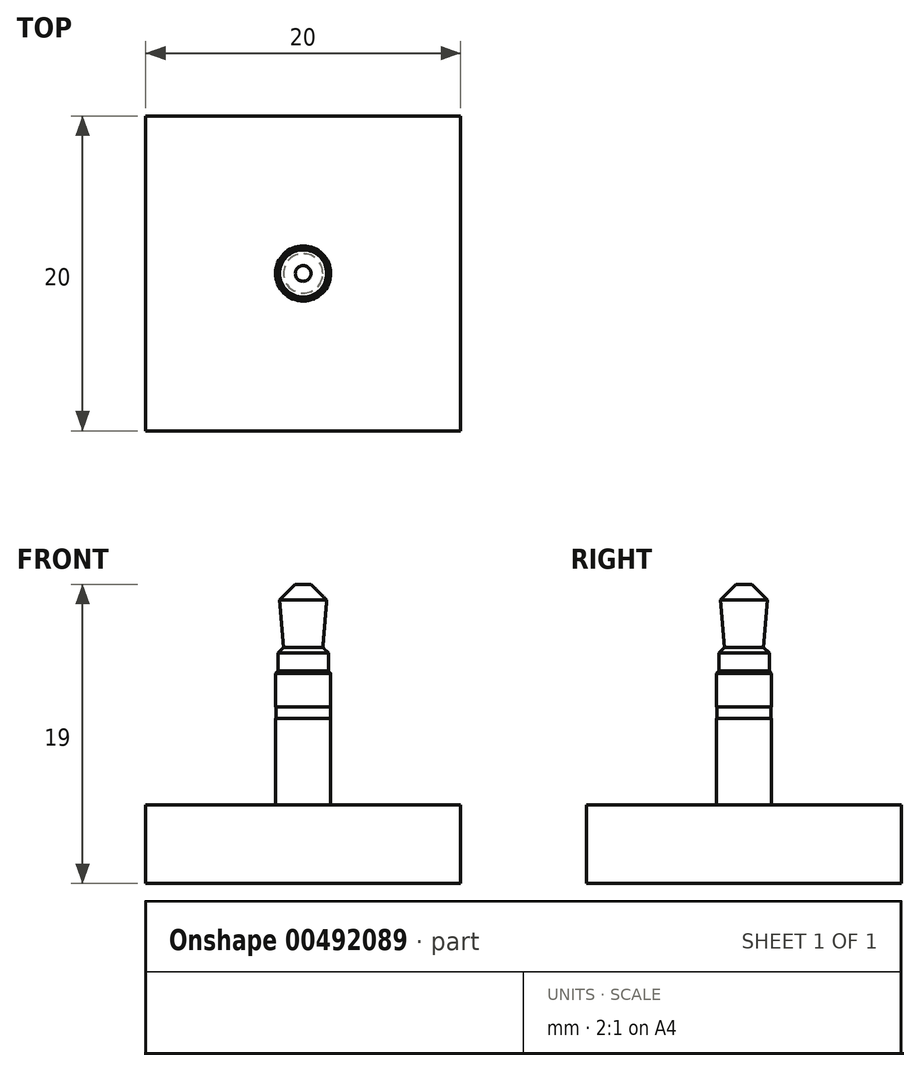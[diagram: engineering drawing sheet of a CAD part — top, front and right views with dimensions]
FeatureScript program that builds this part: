
annotation { "Feature Type Name" : "Feature", "Feature Type Description" : "" }
export const myFeature = defineFeature(function(context is Context, id is Id, definition is map)
    precondition{}
    {
        {
            var Q0;
            Q0=qCreatedBy(makeId("Top.planeOp"),FACE);
            var sketch = newSketch(context, id + "F0", { "sketchPlane" : qUnion([Q0])});
            skCircle(sketch, "E0", {"center": v(0, 0) * mm, "radius": 1.75 * mm});
            skSolve(sketch);
        }
        {
            var Q0;
            Q0=qSketchRegion(id+"F0",true);
            extrude(context, id + "F1", {"entities" : qUnion([Q0]), "depth" : 5.5 * mm});
        }
        {
            var Q0;
            Q0=makeQuery(id+"F1.opExtrude","CAP_FACE",FACE,{"disambiguationData":[OSD([sQuery(id+"F0.wireOp",EDGE,"E0")])],"isStart":false});
            cPlane(context, id + "F2", {"entities" : qUnion([Q0]), "cplaneType" : CPlaneType.OFFSET, "offset" : 0 * mm, "width" : 150 * mm, "height" : 150 * mm});
        }
        {
            var Q0;
            Q0=qCreatedBy(id+"F2.planeOp",FACE);
            var sketch = newSketch(context, id + "F3", { "sketchPlane" : qUnion([Q0])});
            skCircle(sketch, "E1", {"center": v(0, 0) * mm, "radius": 1.73 * mm});
            skSolve(sketch);
        }
        {
            var Q0;
            Q0=qSketchRegion(id+"F3",true);
            extrude(context, id + "F4", {"entities" : qUnion([Q0]), "operationType" : NewBodyOperationType.ADD, "depth" : 0.7 * mm});
        }
        {
            var Q0;
            Q0=makeQuery(id+"F4.opExtrude","CAP_FACE",FACE,{"disambiguationData":[OSD([sQuery(id+"F3.wireOp",EDGE,"E1")])],"isStart":false});
            cPlane(context, id + "F5", {"entities" : qUnion([Q0]), "cplaneType" : CPlaneType.OFFSET, "offset" : 0 * mm, "width" : 150 * mm, "height" : 150 * mm});
        }
        {
            var Q0;
            Q0=qCreatedBy(id+"F5.planeOp",FACE);
            var sketch = newSketch(context, id + "F6", { "sketchPlane" : qUnion([Q0])});
            skCircle(sketch, "E2", {"center": v(0, 0) * mm, "radius": 1.75 * mm});
            skSolve(sketch);
        }
        {
            var Q0;
            Q0=qSketchRegion(id+"F6",true);
            extrude(context, id + "F7", {"entities" : qUnion([Q0]), "operationType" : NewBodyOperationType.ADD, "depth" : 2.3 * mm});
        }
        {
            var Q0;
            Q0=makeQuery(id+"F7.opExtrude","CAP_FACE",FACE,{"disambiguationData":[OSD([sQuery(id+"F6.wireOp",EDGE,"E2")])],"isStart":false});
            cPlane(context, id + "F8", {"entities" : qUnion([Q0]), "cplaneType" : CPlaneType.OFFSET, "offset" : 0 * mm, "width" : 150 * mm, "height" : 150 * mm});
        }
        {
            var Q0;
            Q0=qCreatedBy(id+"F8.planeOp",FACE);
            var sketch = newSketch(context, id + "F9", { "sketchPlane" : qUnion([Q0])});
            skCircle(sketch, "E3", {"center": v(0, 0) * mm, "radius": 1.6 * mm});
            skSolve(sketch);
        }
        {
            var Q0;
            Q0=qSketchRegion(id+"F9",true);
            extrude(context, id + "F10", {"entities" : qUnion([Q0]), "operationType" : NewBodyOperationType.ADD, "depth" : 0.7 * mm});
        }
        {
            var Q0;
            Q0=makeQuery(id+"F10.opExtrude","CAP_FACE",FACE,{"disambiguationData":[OSD([sQuery(id+"F9.wireOp",EDGE,"E3")])],"isStart":false});
            cPlane(context, id + "F11", {"entities" : qUnion([Q0]), "cplaneType" : CPlaneType.OFFSET, "offset" : 0 * mm, "width" : 150 * mm, "height" : 150 * mm});
        }
        {
            var Q0;
            Q0=qCreatedBy(id+"F11.planeOp",FACE);
            var sketch = newSketch(context, id + "F12", { "sketchPlane" : qUnion([Q0])});
            skCircle(sketch, "E4", {"center": v(0, 0) * mm, "radius": 1.6 * mm});
            skSolve(sketch);
        }
        {
            var Q0;
            Q0=qSketchRegion(id+"F12",true);
            extrude(context, id + "F13", {"entities" : qUnion([Q0]), "operationType" : NewBodyOperationType.ADD, "depth" : 0.8 * mm});
        }
        {
            var Q0;
            Q0=makeQuery(id+"F13.opExtrude","CAP_FACE",FACE,{"disambiguationData":[OSD([sQuery(id+"F12.wireOp",EDGE,"E4")])],"isStart":false});
            cPlane(context, id + "F14", {"entities" : qUnion([Q0]), "cplaneType" : CPlaneType.OFFSET, "offset" : 0 * mm, "width" : 150 * mm, "height" : 150 * mm});
        }
        {
            var Q0;
            Q0=qCreatedBy(id+"F14.planeOp",FACE);
            var sketch = newSketch(context, id + "F15", { "sketchPlane" : qUnion([Q0])});
            skCircle(sketch, "E5", {"center": v(0, 0) * mm, "radius": 1.25 * mm});
            skSolve(sketch);
        }
        {
            var Q0;
            Q0=makeQuery(id+"F15.imprint","IMPRINT",FACE,{"disambiguationData":[TD([[makeQuery(id+"F15.imprint","IMPRINT",EDGE,{"derivedFrom":sQuery(id+"F15.wireOp",EDGE,"E5")}),1.0]])]});
            cPlane(context, id + "F16", {"entities" : qUnion([Q0]), "cplaneType" : CPlaneType.OFFSET, "offset" : 3 * mm, "width" : 150 * mm, "height" : 150 * mm});
        }
        {
            var Q0;
            Q0=qCreatedBy(id+"F16.planeOp",FACE);
            var sketch = newSketch(context, id + "F17", { "sketchPlane" : qUnion([Q0])});
            skCircle(sketch, "E6", {"center": v(0, 0) * mm, "radius": 1.5 * mm});
            skSolve(sketch);
        }
        {
            var Q1;
            Q1=makeQuery(id+"F15.imprint","IMPRINT",FACE,{"disambiguationData":[TD([[makeQuery(id+"F15.imprint","IMPRINT",EDGE,{"derivedFrom":sQuery(id+"F15.wireOp",EDGE,"E5")}),1.0]])]});
            var Q2;
            Q2=makeQuery(id+"F17.imprint","IMPRINT",FACE,{"disambiguationData":[TD([[makeQuery(id+"F17.imprint","IMPRINT",EDGE,{"derivedFrom":sQuery(id+"F17.wireOp",EDGE,"E6")}),1.0]])]});
            loft(context, id + "F18", {"operationType" : NewBodyOperationType.ADD, "sheetProfilesArray" : [{ "sheetProfileEntities" : qUnion([Q1]) }, { "sheetProfileEntities" : qUnion([Q2]) }]});
        }
        {
            var Q0;
            Q0=makeQuery(id+"F18.opLoft","CAP_FACE",FACE,{"disambiguationData":[OSD([makeQuery(id+"F17.imprint","IMPRINT",FACE,{"disambiguationData":[TD([[makeQuery(id+"F17.imprint","IMPRINT",EDGE,{"derivedFrom":sQuery(id+"F17.wireOp",EDGE,"E6")}),1.0]])]})])],"isStart":true});
            cPlane(context, id + "F19", {"entities" : qUnion([Q0]), "cplaneType" : CPlaneType.OFFSET, "offset" : 0 * mm, "width" : 150 * mm, "height" : 150 * mm});
        }
        {
            var Q0;
            Q0=qCreatedBy(id+"F19.planeOp",FACE);
            var sketch = newSketch(context, id + "F20", { "sketchPlane" : qUnion([Q0])});
            skCircle(sketch, "E7", {"center": v(0, 0) * mm, "radius": 1.5 * mm});
            skSolve(sketch);
        }
        {
            var Q0;
            Q0=qSketchRegion(id+"F20",true);
            extrude(context, id + "F21", {"entities" : qUnion([Q0]), "operationType" : NewBodyOperationType.ADD, "depth" : 1 * mm});
        }
        {
            var Q0;
            Q0=makeQuery(id+"F21.opExtrude","CAP_EDGE",EDGE,{"disambiguationData":[OSD([sQuery(id+"F20.wireOp",EDGE,"E7")])],"isStart":false});
            chamfer(context, id + "F22", {"entities" : qUnion([Q0]), "chamferType" : ChamferType.OFFSET_ANGLE, "width" : 1 * mm, "oppositeDirection" : false, "angle" : 45 * degree, "tangentPropagation" : true});
        }
        {
            var Q0;
            Q0=makeQuery(id+"F7.opExtrude","CAP_EDGE",EDGE,{"disambiguationData":[OSD([sQuery(id+"F6.wireOp",EDGE,"E2")])],"isStart":false});
            chamfer(context, id + "F23", {"entities" : qUnion([Q0]), "width" : 0.15 * mm, "tangentPropagation" : true});
        }
        {
            var Q0;
            Q0=makeQuery(id+"F13.opExtrude","CAP_EDGE",EDGE,{"disambiguationData":[OSD([sQuery(id+"F12.wireOp",EDGE,"E4")])],"isStart":false});
            chamfer(context, id + "F24", {"entities" : qUnion([Q0]), "width" : 0.35 * mm, "tangentPropagation" : true});
        }
        {
            var Q0;
            Q0=makeQuery(id+"F1.opExtrude","CAP_FACE",FACE,{"disambiguationData":[OSD([sQuery(id+"F0.wireOp",EDGE,"E0")])],"isStart":true});
            cPlane(context, id + "F25", {"entities" : qUnion([Q0]), "cplaneType" : CPlaneType.OFFSET, "offset" : 0 * mm, "width" : 150 * mm, "height" : 150 * mm});
        }
        {
            var Q0;
            Q0=qCreatedBy(id+"F25.planeOp",FACE);
            var sketch = newSketch(context, id + "F26", { "sketchPlane" : qUnion([Q0])});
            skLineSegment(sketch, "E8.bottom", {"start": v(10, 10) * mm, "end": v(-10, 10) * mm});
            skLineSegment(sketch, "E8.top", {"start": v(10, -10) * mm, "end": v(-10, -10) * mm});
            skLineSegment(sketch, "E8.left", {"start": v(10, 10) * mm, "end": v(10, -10) * mm});
            skLineSegment(sketch, "E8.right", {"start": v(-10, 10) * mm, "end": v(-10, -10) * mm});
            skPoint(sketch, "E8.middle", {"position": v(0, 0) * mm});
            skSolve(sketch);
        }
        {
            var Q0;
            Q0 = qSketchRegion(id + "F26", true);
            extrude(context, id + "F27", {"entities" : qUnion([Q0]), "operationType" : NewBodyOperationType.ADD, "depth" : 5 * mm});
        }
    });
